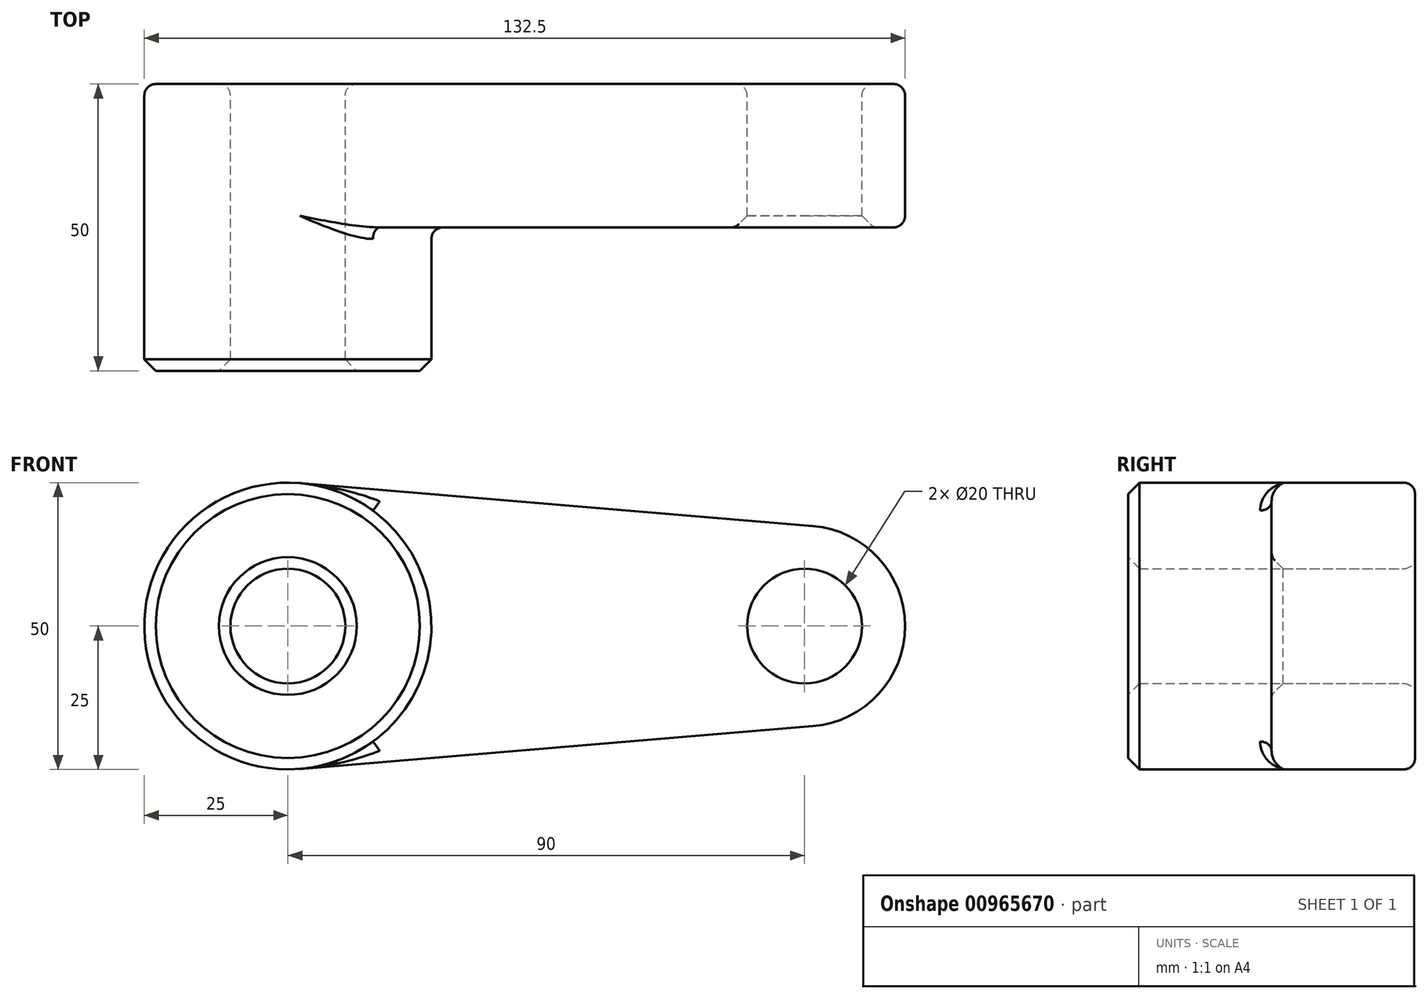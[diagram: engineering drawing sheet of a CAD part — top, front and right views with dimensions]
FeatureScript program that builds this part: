
annotation { "Feature Type Name" : "Feature", "Feature Type Description" : "" }
export const myFeature = defineFeature(function(context is Context, id is Id, definition is map)
    precondition{}
    {
        {
            var Q0;
            Q0=qCreatedBy(makeId("Front.planeOp"),FACE);
            var sketch = newSketch(context, id + "F0", { "sketchPlane" : qUnion([Q0])});
            skCircle(sketch, "E0", {"center": v(0, 0) * mm, "radius": 25 * mm});
            skCircle(sketch, "E1", {"center": v(90, 0) * mm, "radius": 17.5 * mm});
            skLineSegment(sketch, "E2", {"start": v(2.08, -24.91) * mm, "end": v(91.46, -17.44) * mm});
            skLineSegment(sketch, "E3", {"start": v(2.08, 24.91) * mm, "end": v(91.46, 17.44) * mm});
            skCircle(sketch, "E4", {"center": v(0, 0) * mm, "radius": 10 * mm});
            skCircle(sketch, "E5", {"center": v(90, 0) * mm, "radius": 10 * mm});
            skSolve(sketch);
        }
        {
            var Q0;
            Q0 = qSketchRegion(id + "F0", true);
            extrude(context, id + "F1", {"entities" : qUnion([Q0]), "depth" : 25 * mm, "offsetDistance" : 25 * mm});
        }
        {
            var Q0;
            Q0=makeQuery(id+"F0.imprint","IMPRINT",FACE,{"disambiguationData":[TD([[makeQuery(id+"F0.imprint","IMPRINT",EDGE,{"derivedFrom":sQuery(id+"F0.wireOp",EDGE,"E4")}),-1.0]])]});
            extrude(context, id + "F2", {"entities" : qUnion([Q0]), "operationType" : NewBodyOperationType.ADD, "depth" : 50 * mm, "offsetDistance" : 25 * mm});
        }
        {
            var Q0;
            Q0=makeQuery(id+"F2.opExtrude","CAP_EDGE",EDGE,{"disambiguationData":[OSD([sQuery(id+"F0.wireOp",EDGE,"E4")])],"isStart":false});
            var Q1;
            Q1=makeQuery(id+"F2.opExtrude","CAP_EDGE",EDGE,{"disambiguationData":[OSD([sQuery(id+"F0.wireOp",EDGE,"E0")])],"isStart":false});
            var Q2;
            Q2=makeQuery(id+"F1.opExtrude","CAP_EDGE",EDGE,{"disambiguationData":[OSD([sQuery(id+"F0.wireOp",EDGE,"E5")])],"isStart":false});
            chamfer(context, id + "F3", {"entities" : qUnion([Q0, Q1, Q2]), "width" : 2 * mm, "tangentPropagation" : true});
        }
        {
            var Q0;
            Q0=makeQuery(id+"F1.opExtrude","CAP_FACE",FACE,{"disambiguationData":[OSD([sQuery(id+"F0.wireOp",EDGE,"E0"),sQuery(id+"F0.wireOp",EDGE,"E1"),sQuery(id+"F0.wireOp",EDGE,"E2"),sQuery(id+"F0.wireOp",EDGE,"E3"),sQuery(id+"F0.wireOp",EDGE,"E4"),sQuery(id+"F0.wireOp",EDGE,"E5")])],"isStart":true});
            var Q1;
            Q1=makeQuery(id+"F1.opExtrude","CAP_FACE",FACE,{"disambiguationData":[OSD([sQuery(id+"F0.wireOp",EDGE,"E0"),sQuery(id+"F0.wireOp",EDGE,"E1"),sQuery(id+"F0.wireOp",EDGE,"E2"),sQuery(id+"F0.wireOp",EDGE,"E3"),sQuery(id+"F0.wireOp",EDGE,"E4"),sQuery(id+"F0.wireOp",EDGE,"E5")])],"isStart":false});
            fillet(context, id + "F4", {"entities" : qUnion([Q0, Q1]), "radius" : 2 * mm, "tangentPropagation" : true, "allowEdgeOverflow" : false});
        }
    });
